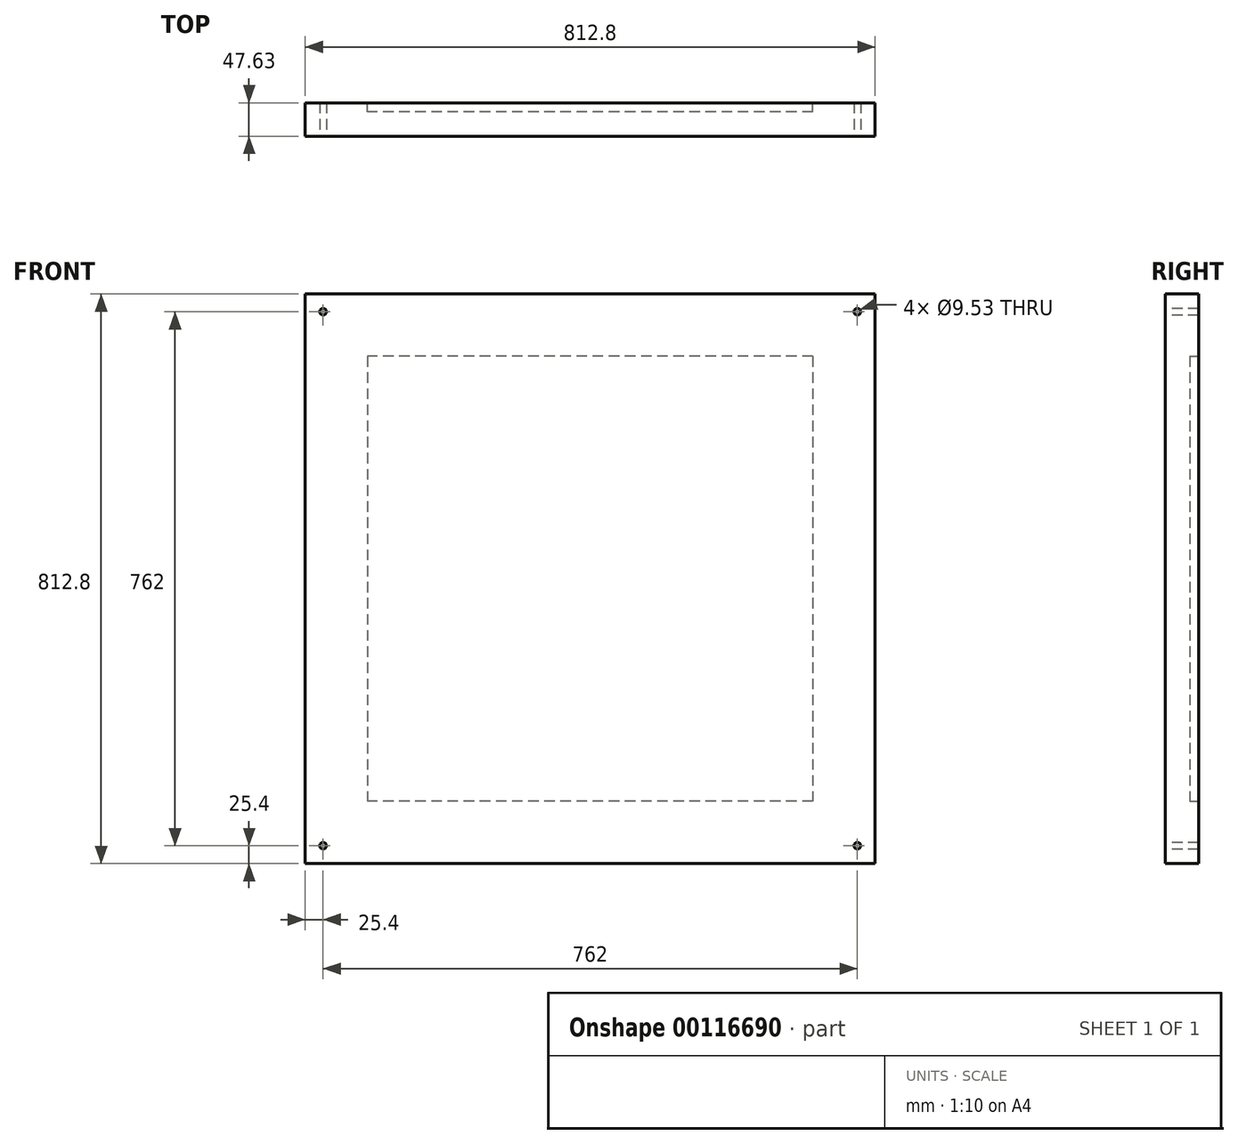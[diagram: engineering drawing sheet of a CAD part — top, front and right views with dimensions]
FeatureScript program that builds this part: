
annotation { "Feature Type Name" : "Feature", "Feature Type Description" : "" }
export const myFeature = defineFeature(function(context is Context, id is Id, definition is map)
    precondition{}
    {
        {
            var Q0;
            Q0=qCreatedBy(makeId("Front.planeOp"),FACE);
            var sketch = newSketch(context, id + "F0", { "sketchPlane" : qUnion([Q0])});
            skLineSegment(sketch, "E0.bottom", {"start": v(406.4, 406.4) * mm, "end": v(-406.4, 406.4) * mm});
            skLineSegment(sketch, "E0.top", {"start": v(406.4, -406.4) * mm, "end": v(-406.4, -406.4) * mm});
            skLineSegment(sketch, "E0.left", {"start": v(406.4, 406.4) * mm, "end": v(406.4, -406.4) * mm});
            skLineSegment(sketch, "E0.right", {"start": v(-406.4, 406.4) * mm, "end": v(-406.4, -406.4) * mm});
            skPoint(sketch, "E0.middle", {"position": v(0, 0) * mm});
            skLineSegment(sketch, "E1.bottom", {"start": v(317.5, 317.5) * mm, "end": v(-317.5, 317.5) * mm});
            skLineSegment(sketch, "E1.top", {"start": v(317.5, -317.5) * mm, "end": v(-317.5, -317.5) * mm});
            skLineSegment(sketch, "E1.left", {"start": v(317.5, 317.5) * mm, "end": v(317.5, -317.5) * mm});
            skLineSegment(sketch, "E1.right", {"start": v(-317.5, 317.5) * mm, "end": v(-317.5, -317.5) * mm});
            skSolve(sketch);
        }
        {
            var Q0;
            Q0=makeQuery(id+"F0.imprint","IMPRINT",FACE,{"disambiguationData":[TD([[makeQuery(id+"F0.imprint","IMPRINT",EDGE,{"derivedFrom":sQuery(id+"F0.wireOp",EDGE,"E0.bottom")}),1.0]])]});
            extrude(context, id + "F1", {"entities" : qUnion([Q0]), "depth" : 38.1 * mm});
        }
        {
            var Q0;
            Q0=qCreatedBy(makeId("Front.planeOp"),FACE);
            var sketch = newSketch(context, id + "F2", { "sketchPlane" : qUnion([Q0])});
            skLineSegment(sketch, "E2.bottom", {"start": v(405.63, 406.4) * mm, "end": v(-405.63, 406.4) * mm});
            skLineSegment(sketch, "E2.top", {"start": v(405.63, -406.4) * mm, "end": v(-405.63, -406.4) * mm});
            skLineSegment(sketch, "E2.left", {"start": v(405.63, 406.4) * mm, "end": v(405.63, -406.4) * mm});
            skLineSegment(sketch, "E2.right", {"start": v(-405.63, 406.4) * mm, "end": v(-405.63, -406.4) * mm});
            skPoint(sketch, "E2.middle", {"position": v(0, 0) * mm});
            skSolve(sketch);
        }
        {
            var Q0;
            Q0=makeQuery(id+"F1.opExtrude","CAP_FACE",FACE,{"disambiguationData":[OSD([sQuery(id+"F0.wireOp",EDGE,"E0.bottom"),sQuery(id+"F0.wireOp",EDGE,"E0.top"),sQuery(id+"F0.wireOp",EDGE,"E0.left"),sQuery(id+"F0.wireOp",EDGE,"E0.right"),sQuery(id+"F0.wireOp",EDGE,"E1.bottom"),sQuery(id+"F0.wireOp",EDGE,"E1.top"),sQuery(id+"F0.wireOp",EDGE,"E1.left"),sQuery(id+"F0.wireOp",EDGE,"E1.right")])],"isStart":false});
            var sketch = newSketch(context, id + "F3", { "sketchPlane" : qUnion([Q0])});
            skLineSegment(sketch, "E3.bottom", {"start": v(406.4, 406.4) * mm, "end": v(-406.4, 406.4) * mm});
            skLineSegment(sketch, "E3.top", {"start": v(406.4, -406.4) * mm, "end": v(-406.4, -406.4) * mm});
            skLineSegment(sketch, "E3.left", {"start": v(406.4, 406.4) * mm, "end": v(406.4, -406.4) * mm});
            skLineSegment(sketch, "E3.right", {"start": v(-406.4, 406.4) * mm, "end": v(-406.4, -406.4) * mm});
            skPoint(sketch, "E3.middle", {"position": v(0, 0) * mm});
            skSolve(sketch);
        }
        {
            var Q0;
            Q0 = qSketchRegion(id + "F3", true);
            extrude(context, id + "F4", {"entities" : qUnion([Q0]), "operationType" : NewBodyOperationType.ADD, "depth" : 9.52 * mm, "hasSecondDirection" : true, "secondDirectionOppositeDirection" : true, "secondDirectionDepth" : 25.4 * mm});
        }
        {
            var Q0;
            Q0=makeQuery(id+"F4.opExtrude","CAP_FACE",FACE,{"disambiguationData":[OSD([sQuery(id+"F3.wireOp",EDGE,"E3.bottom"),sQuery(id+"F3.wireOp",EDGE,"E3.top"),sQuery(id+"F3.wireOp",EDGE,"E3.left"),sQuery(id+"F3.wireOp",EDGE,"E3.right")])],"isStart":false});
            var sketch = newSketch(context, id + "F5", { "sketchPlane" : qUnion([Q0])});
            skLineSegment(sketch, "E4.bottom", {"start": v(381, 381) * mm, "end": v(-381, 381) * mm, "construction": true});
            skLineSegment(sketch, "E4.top", {"start": v(381, -381) * mm, "end": v(-381, -381) * mm, "construction": true});
            skLineSegment(sketch, "E4.left", {"start": v(381, 381) * mm, "end": v(381, -381) * mm, "construction": true});
            skLineSegment(sketch, "E4.right", {"start": v(-381, 381) * mm, "end": v(-381, -381) * mm, "construction": true});
            skPoint(sketch, "E4.middle", {"position": v(0, 0) * mm});
            skCircle(sketch, "E5", {"center": v(381, 381) * mm, "radius": 4.76 * mm});
            skCircle(sketch, "E6", {"center": v(381, -381) * mm, "radius": 4.76 * mm});
            skCircle(sketch, "E7", {"center": v(-381, -381) * mm, "radius": 4.76 * mm});
            skCircle(sketch, "E8", {"center": v(-381, 381) * mm, "radius": 4.76 * mm});
            skSolve(sketch);
        }
        {
            var Q0;
            Q0=makeQuery(id+"F5.imprint","IMPRINT",FACE,{"disambiguationData":[TD([[makeQuery(id+"F5.imprint","IMPRINT",EDGE,{"derivedFrom":sQuery(id+"F5.wireOp",EDGE,"E7")}),1.0]])]});
            var Q1;
            Q1=makeQuery(id+"F5.imprint","IMPRINT",FACE,{"disambiguationData":[TD([[makeQuery(id+"F5.imprint","IMPRINT",EDGE,{"derivedFrom":sQuery(id+"F5.wireOp",EDGE,"E6")}),1.0]])]});
            var Q2;
            Q2=makeQuery(id+"F5.imprint","IMPRINT",FACE,{"disambiguationData":[TD([[makeQuery(id+"F5.imprint","IMPRINT",EDGE,{"derivedFrom":sQuery(id+"F5.wireOp",EDGE,"E5")}),1.0]])]});
            var Q3;
            Q3=makeQuery(id+"F5.imprint","IMPRINT",FACE,{"disambiguationData":[TD([[makeQuery(id+"F5.imprint","IMPRINT",EDGE,{"derivedFrom":sQuery(id+"F5.wireOp",EDGE,"E8")}),1.0]])]});
            extrude(context, id + "F6", {"entities" : qUnion([Q0, Q1, Q2, Q3]), "operationType" : NewBodyOperationType.REMOVE, "oppositeDirection" : true, "depth" : 254 * mm});
        }
    });
